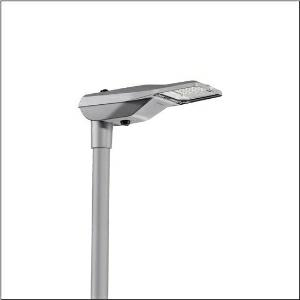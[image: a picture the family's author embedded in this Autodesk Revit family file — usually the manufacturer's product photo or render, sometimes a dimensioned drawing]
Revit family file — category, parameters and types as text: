
# Revit family: streetlight_sl_21_iq_micro___p0_8a_5xe1u31y08db_9c46
name_source: partatom
category: Lighting Fixtures
units: mm (PartAtom-declared; Revit-internal decimal feet)

## family parameters
Cut with Voids When Loaded = No
Host = Face
Light Source = No
Part Type = Normal
Room Calculation Point = No
Round Connector Dimension = Use Diameter
Shared = No

## types (1)
- --- (1 x LED, 5130 lm, 39.1 W, 3000K)
    Apparent Load = 39 VA
    CIE Flux Codes = 33 69 96 100 100
    Color Rendering = 70
    Color Temperature = 3000K
    Default Elevation = 1800 mm
    Description = Streetlight SL 21 iQ micro, mast luminaire, primary light control with lens, of PMMA, primary optical cover: cover, of toughened safety glass, transparent, light distribution: P0.8a, light emission: direct distribution, primary light characteristic: asymmetric, installation type: post-top, side-entry, LED, High Power LED, rated luminous flux: 5.130lm, luminous efficacy: 131lm/W, light colour: 730, colour temperature: 3000K, control gear: iQ-Street Remote, D4i with power reduction, control: pre-setting: logarithmic dimming characteristic, Street-Remote, Auto-Match, Temp-Guard, Lumen-Switch, Night-Set, Smart-Wire, Light-Fading, Desk-Remote (wireless, voltage-free reading and setting of iQ features in the workshop via application-optimized NFC function/RFID function), optimised constant luminous flux control (CLO 2.0), mains connection: 220..240V, AC, 50/60Hz, start of lifetime: 39W, end of service life: 41W, reduction: 17W, luminaire housing, of diecast aluminium, powder-coated, Siteco® metallic grey (DB 702S), corrosivity category C5 mid according to DIN EN ISO 12944, please order mast flange separately, inclination adjustable: 0°, 5°, 10°, 15°, sealing non-destructively replaceable, multi-level sealing system, length: 528mm, width: 235mm, height: 110mm, mast flange for spigot size: 42mm (side-entry): 5XC10008XM4, 60/48mm (side-entry/post-top): 5XC10108XM2, 76/60mm (side-entry/post-top): 5XC10108XM1, mounting height: 4..8m, Smart Interface below and above, protection rating (complete): IP66, insulation class (complete): insulation class II (safety insulation), certification: CE, ENEC, ENEC+, VDE, impact resistance: IK10, permissible operating ambient temperature for outdoor applications: -40..+50°C, standard-compliant lighting for roads and squares, packaging unit: 1 piece

Light Distribution: P0.8a
    Height = 110 mm
    Lamp = 1 x LED
    Lamp Light Flux = 5130 lm
    Lamp Power = 39.1 W
    Lamp count = 1
    Length = 528 mm
    Luminous efficacy = 131 lm/W
    Manufacturer = Siteco
    ModVariant = No
    Model = 5XE1U31Y08DB
    Number of Poles = 1
    OnlyDefault = Yes
    Power Factor = 1
    Product Name = Streetlight SL 21 iQ micro | P0.8a
    Product group = mast luminaire | pylon top
    ProductGroupID = 6100
    Protection Class = Protection class II
    Protection Degree = IP 66
    RLX_Detail_Level = 1
    RLX_Emergency_Light_Flux = 0 lm
    RLX_Emergency_Type = 0
    RLX_Emergency_Type_DB = No
    RlxData = <blob elided: 99589 chars, md5=e8bb5ab8>
    Socket = socket
    Standby Power = 0 W
    System Light Flux = 5130 lm
    System Power = 39 W
    Type Comments = factory setting: luminous flux: 100 % | dim-lin: 254 | 765 mA
    Type Image = l_1007239.jpg
    URL = http://relux.com
    VarID = @adj_074256
    Voltage = 0 V
    Weight = 0.00 kg
    Width = 235 mm

## geometry (parser evidence)
native form markers: Blend x4, Sweep x11
no freeform markers — native parametric forms only
